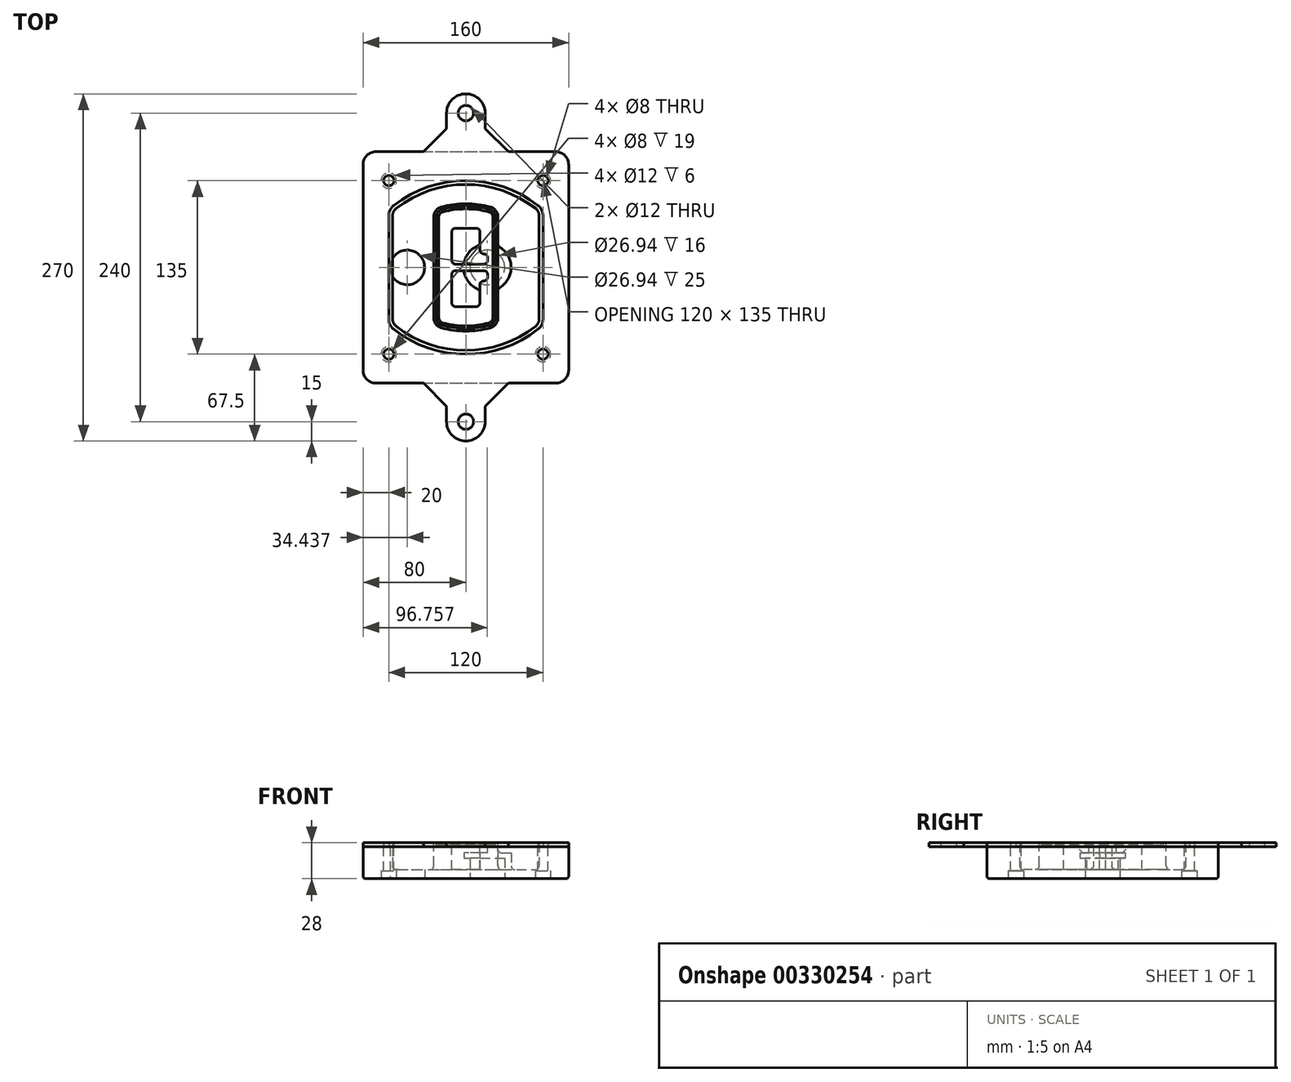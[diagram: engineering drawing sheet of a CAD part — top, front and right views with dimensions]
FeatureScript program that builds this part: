
annotation { "Feature Type Name" : "Feature", "Feature Type Description" : "" }
export const myFeature = defineFeature(function(context is Context, id is Id, definition is map)
    precondition{}
    {
        {
            var Q0;
            Q0=qCreatedBy(makeId("Top.planeOp"),FACE);
            var sketch = newSketch(context, id + "F0", { "sketchPlane" : qUnion([Q0])});
            skPoint(sketch, "E0.rect.middle", {"position": v(0, 0) * mm});
            skLineSegment(sketch, "E1.bottom", {"start": v(-70, -90) * mm, "end": v(70, -90) * mm});
            skLineSegment(sketch, "E1.top", {"start": v(-70, 90) * mm, "end": v(70, 90) * mm});
            skLineSegment(sketch, "E1.left", {"start": v(-80, -80) * mm, "end": v(-80, 80) * mm});
            skLineSegment(sketch, "E1.right", {"start": v(80, -80) * mm, "end": v(80, 80) * mm});
            skLineSegment(sketch, "E2", {"start": v(-80, 90) * mm, "end": v(80, -90) * mm, "construction": true});
            skLineSegment(sketch, "E3", {"start": v(80, 90) * mm, "end": v(-80, -90) * mm, "construction": true});
            skCircle(sketch, "E4", {"center": v(-60, 67.5) * mm, "radius": 4 * mm});
            skCircle(sketch, "E5", {"center": v(60, 67.5) * mm, "radius": 4 * mm});
            skCircle(sketch, "E6", {"center": v(60, -67.5) * mm, "radius": 4 * mm});
            skCircle(sketch, "E7", {"center": v(-60, -67.5) * mm, "radius": 4 * mm});
            skLineSegment(sketch, "E8", {"start": v(-60, 67.5) * mm, "end": v(60, 67.5) * mm, "construction": true});
            skLineSegment(sketch, "E9", {"start": v(60, 67.5) * mm, "end": v(60, -67.5) * mm, "construction": true});
            skLineSegment(sketch, "E10", {"start": v(60, -67.5) * mm, "end": v(-60, -67.5) * mm, "construction": true});
            skLineSegment(sketch, "E11", {"start": v(-60, -67.5) * mm, "end": v(-60, 67.5) * mm, "construction": true});
            skLineSegment(sketch, "E12", {"start": v(-60, 40.3) * mm, "end": v(-60, -40.3) * mm});
            skLineSegment(sketch, "E13", {"start": v(60, 40.3) * mm, "end": v(60, -40.3) * mm});
            skArc(sketch, "E14", {"start": v(56.15, 48.18) * mm, "mid": v(0, 67.5) * mm, "end": v(-56.15, 48.18) * mm});
            skArc(sketch, "E15", {"start": v(-56.15, -48.18) * mm, "mid": v(0, -67.5) * mm, "end": v(56.15, -48.18) * mm});
            skLineSegment(sketch, "E16", {"start": v(-60, 0) * mm, "end": v(60, 0) * mm, "construction": true});
            skPoint(sketch, "E17.visualSharp", {"position": v(-60, -45) * mm});
            skArc(sketch, "E17.filletArc", {"start": v(-60, -40.3) * mm, "mid": v(-58.99, -44.68) * mm, "end": v(-56.15, -48.18) * mm});
            skPoint(sketch, "E18.visualSharp", {"position": v(-60, 45) * mm});
            skArc(sketch, "E18.filletArc", {"start": v(-56.15, 48.18) * mm, "mid": v(-58.99, 44.68) * mm, "end": v(-60, 40.3) * mm});
            skPoint(sketch, "E19.visualSharp", {"position": v(60, 45) * mm});
            skArc(sketch, "E19.filletArc", {"start": v(60, 40.3) * mm, "mid": v(58.99, 44.68) * mm, "end": v(56.15, 48.18) * mm});
            skPoint(sketch, "E20.visualSharp", {"position": v(60, -45) * mm});
            skArc(sketch, "E20.filletArc", {"start": v(56.15, -48.18) * mm, "mid": v(58.99, -44.68) * mm, "end": v(60, -40.3) * mm});
            skPoint(sketch, "E21.visualSharp", {"position": v(-80, 90) * mm});
            skArc(sketch, "E21.filletArc", {"start": v(-70, 90) * mm, "mid": v(-77.07, 87.07) * mm, "end": v(-80, 80) * mm});
            skPoint(sketch, "E22.visualSharp", {"position": v(80, 90) * mm});
            skArc(sketch, "E22.filletArc", {"start": v(80, 80) * mm, "mid": v(77.07, 87.07) * mm, "end": v(70, 90) * mm});
            skPoint(sketch, "E23.visualSharp", {"position": v(80, -90) * mm});
            skArc(sketch, "E23.filletArc", {"start": v(70, -90) * mm, "mid": v(77.07, -87.07) * mm, "end": v(80, -80) * mm});
            skPoint(sketch, "E24.visualSharp", {"position": v(-80, -90) * mm});
            skArc(sketch, "E24.filletArc", {"start": v(-80, -80) * mm, "mid": v(-77.07, -87.07) * mm, "end": v(-70, -90) * mm});
            skArc(sketch, "E25.0", {"start": v(57, 40.3) * mm, "mid": v(56.3, 43.36) * mm, "end": v(54.3, 45.81) * mm});
            skLineSegment(sketch, "E25.1", {"start": v(57, 40.3) * mm, "end": v(57, -40.3) * mm});
            skArc(sketch, "E25.2", {"start": v(54.3, -45.81) * mm, "mid": v(56.3, -43.36) * mm, "end": v(57, -40.3) * mm});
            skArc(sketch, "E25.3", {"start": v(-54.3, -45.81) * mm, "mid": v(0, -64.5) * mm, "end": v(54.3, -45.81) * mm});
            skArc(sketch, "E25.4", {"start": v(-57, -40.3) * mm, "mid": v(-56.3, -43.36) * mm, "end": v(-54.3, -45.81) * mm});
            skArc(sketch, "E25.5", {"start": v(54.3, 45.81) * mm, "mid": v(0, 64.5) * mm, "end": v(-54.3, 45.81) * mm});
            skLineSegment(sketch, "E25.6", {"start": v(-57, 40.3) * mm, "end": v(-57, -40.3) * mm});
            skArc(sketch, "E25.7", {"start": v(-54.3, 45.81) * mm, "mid": v(-56.3, 43.36) * mm, "end": v(-57, 40.3) * mm});
            skArc(sketch, "E26.0", {"start": v(-58.62, 51.33) * mm, "mid": v(-62.58, 46.43) * mm, "end": v(-64, 40.3) * mm});
            skArc(sketch, "E26.1", {"start": v(58.62, 51.33) * mm, "mid": v(0, 71.5) * mm, "end": v(-58.62, 51.33) * mm});
            skArc(sketch, "E26.2", {"start": v(64, 40.3) * mm, "mid": v(62.58, 46.43) * mm, "end": v(58.62, 51.33) * mm});
            skLineSegment(sketch, "E26.3", {"start": v(64, 40.3) * mm, "end": v(64, -40.3) * mm});
            skArc(sketch, "E26.4", {"start": v(58.62, -51.33) * mm, "mid": v(62.58, -46.43) * mm, "end": v(64, -40.3) * mm});
            skLineSegment(sketch, "E26.5", {"start": v(-64, 40.3) * mm, "end": v(-64, -40.3) * mm});
            skArc(sketch, "E26.6", {"start": v(-58.62, -51.33) * mm, "mid": v(0, -71.5) * mm, "end": v(58.62, -51.33) * mm});
            skArc(sketch, "E26.7", {"start": v(-64, -40.3) * mm, "mid": v(-62.58, -46.43) * mm, "end": v(-58.62, -51.33) * mm});
            skSolve(sketch);
        }
        {
            var Q0;
            Q0=makeQuery(id+"F0.imprint","IMPRINT",FACE,{"disambiguationData":[TD([[makeQuery(id+"F0.imprint","IMPRINT",EDGE,{"derivedFrom":sQuery(id+"F0.wireOp",EDGE,"E1.bottom")}),1.0]])]});
            var Q1;
            Q1=makeQuery(id+"F0.imprint","IMPRINT",FACE,{"disambiguationData":[TD([[makeQuery(id+"F0.imprint","IMPRINT",EDGE,{"derivedFrom":sQuery(id+"F0.wireOp",EDGE,"E12")}),1.0]])]});
            var Q2;
            Q2=makeQuery(id+"F0.imprint","IMPRINT",FACE,{"disambiguationData":[TD([[makeQuery(id+"F0.imprint","IMPRINT",EDGE,{"derivedFrom":sQuery(id+"F0.wireOp",EDGE,"E25.0")}),1.0]])]});
            var Q3;
            Q3=makeQuery(id+"F0.imprint","IMPRINT",FACE,{"disambiguationData":[TD([[makeQuery(id+"F0.imprint","IMPRINT",EDGE,{"derivedFrom":sQuery(id+"F0.wireOp",EDGE,"E12")}),-1.0]])]});
            extrude(context, id + "F1", {"entities" : qUnion([Q0, Q1, Q2, Q3]), "oppositeDirection" : true, "depth" : 25 * mm});
        }
        {
            var Q0;
            Q0=makeQuery(id+"F0.imprint","IMPRINT",FACE,{"disambiguationData":[TD([[makeQuery(id+"F0.imprint","IMPRINT",EDGE,{"derivedFrom":sQuery(id+"F0.wireOp",EDGE,"E12")}),1.0]])]});
            extrude(context, id + "F2", {"entities" : qUnion([Q0]), "operationType" : NewBodyOperationType.ADD, "depth" : 3 * mm});
        }
        {
            var Q0;
            Q0=makeQuery(id+"F0.imprint","IMPRINT",FACE,{"disambiguationData":[TD([[makeQuery(id+"F0.imprint","IMPRINT",EDGE,{"derivedFrom":sQuery(id+"F0.wireOp",EDGE,"E25.0")}),1.0]])]});
            extrude(context, id + "F3", {"entities" : qUnion([Q0]), "operationType" : NewBodyOperationType.REMOVE, "oppositeDirection" : true, "depth" : 18 * mm});
        }
        {
            var Q0;
            Q0=makeQuery(id+"F2.opExtrude","CAP_FACE",FACE,{"disambiguationData":[OSD([sQuery(id+"F0.wireOp",EDGE,"E12"),sQuery(id+"F0.wireOp",EDGE,"E13"),sQuery(id+"F0.wireOp",EDGE,"E14"),sQuery(id+"F0.wireOp",EDGE,"E15"),sQuery(id+"F0.wireOp",EDGE,"E17.filletArc"),sQuery(id+"F0.wireOp",EDGE,"E18.filletArc"),sQuery(id+"F0.wireOp",EDGE,"E19.filletArc"),sQuery(id+"F0.wireOp",EDGE,"E20.filletArc"),sQuery(id+"F0.wireOp",EDGE,"E25.0"),sQuery(id+"F0.wireOp",EDGE,"E25.1"),sQuery(id+"F0.wireOp",EDGE,"E25.2"),sQuery(id+"F0.wireOp",EDGE,"E25.3"),sQuery(id+"F0.wireOp",EDGE,"E25.4"),sQuery(id+"F0.wireOp",EDGE,"E25.5"),sQuery(id+"F0.wireOp",EDGE,"E25.6"),sQuery(id+"F0.wireOp",EDGE,"E25.7")])],"isStart":false});
            var sketch = newSketch(context, id + "F4", { "sketchPlane" : qUnion([Q0])});
            skArc(sketch, "E27.0", {"start": v(-19.08, -46.97) * mm, "mid": v(0, -49.5) * mm, "end": v(19.08, -46.97) * mm});
            skArc(sketch, "E28.0", {"start": v(19.08, 46.97) * mm, "mid": v(0, 49.5) * mm, "end": v(-19.08, 46.97) * mm});
            skLineSegment(sketch, "E29", {"start": v(-25, 39.25) * mm, "end": v(-25, -39.25) * mm});
            skLineSegment(sketch, "E30", {"start": v(25, 39.25) * mm, "end": v(25, -39.25) * mm});
            skLineSegment(sketch, "E31", {"start": v(-25, 45.1) * mm, "end": v(25, 45.1) * mm, "construction": true});
            skLineSegment(sketch, "E32", {"start": v(-25, -45.1) * mm, "end": v(25, -45.1) * mm, "construction": true});
            skPoint(sketch, "E33.visualSharp", {"position": v(-25, 45.1) * mm});
            skArc(sketch, "E33.filletArc", {"start": v(-19.08, 46.97) * mm, "mid": v(-23.35, 44.11) * mm, "end": v(-25, 39.25) * mm});
            skPoint(sketch, "E34.visualSharp", {"position": v(25, 45.1) * mm});
            skArc(sketch, "E34.filletArc", {"start": v(25, 39.25) * mm, "mid": v(23.35, 44.11) * mm, "end": v(19.08, 46.97) * mm});
            skPoint(sketch, "E35.visualSharp", {"position": v(25, -45.1) * mm});
            skArc(sketch, "E35.filletArc", {"start": v(19.08, -46.97) * mm, "mid": v(23.35, -44.11) * mm, "end": v(25, -39.25) * mm});
            skPoint(sketch, "E36.visualSharp", {"position": v(-25, -45.1) * mm});
            skArc(sketch, "E36.filletArc", {"start": v(-25, -39.25) * mm, "mid": v(-23.35, -44.11) * mm, "end": v(-19.08, -46.97) * mm});
            skArc(sketch, "E37.0", {"start": v(54.3, 45.81) * mm, "mid": v(0, 64.5) * mm, "end": v(-54.3, 45.81) * mm});
            skArc(sketch, "E37.1", {"start": v(-54.3, 45.81) * mm, "mid": v(-56.3, 43.36) * mm, "end": v(-57, 40.3) * mm});
            skLineSegment(sketch, "E37.2", {"start": v(-57, 40.3) * mm, "end": v(-57, -40.3) * mm});
            skArc(sketch, "E37.3", {"start": v(-57, -40.3) * mm, "mid": v(-56.3, -43.36) * mm, "end": v(-54.3, -45.81) * mm});
            skArc(sketch, "E37.4", {"start": v(-54.3, -45.81) * mm, "mid": v(0, -64.5) * mm, "end": v(54.3, -45.81) * mm});
            skArc(sketch, "E37.5", {"start": v(54.3, -45.81) * mm, "mid": v(56.3, -43.36) * mm, "end": v(57, -40.3) * mm});
            skLineSegment(sketch, "E37.6", {"start": v(57, 40.3) * mm, "end": v(57, -40.3) * mm});
            skArc(sketch, "E37.7", {"start": v(57, 40.3) * mm, "mid": v(56.3, 43.36) * mm, "end": v(54.3, 45.81) * mm});
            skLineSegment(sketch, "E38.0", {"start": v(23, 39.25) * mm, "end": v(23, -39.25) * mm});
            skArc(sketch, "E38.1", {"start": v(18.56, -45.04) * mm, "mid": v(21.76, -42.9) * mm, "end": v(23, -39.25) * mm});
            skArc(sketch, "E38.2", {"start": v(-18.56, -45.04) * mm, "mid": v(0, -47.5) * mm, "end": v(18.56, -45.04) * mm});
            skArc(sketch, "E38.3", {"start": v(-23, -39.25) * mm, "mid": v(-21.76, -42.9) * mm, "end": v(-18.56, -45.04) * mm});
            skLineSegment(sketch, "E38.4", {"start": v(-23, 39.25) * mm, "end": v(-23, -39.25) * mm});
            skArc(sketch, "E38.5", {"start": v(23, 39.25) * mm, "mid": v(21.76, 42.9) * mm, "end": v(18.56, 45.04) * mm});
            skArc(sketch, "E38.6", {"start": v(-18.56, 45.04) * mm, "mid": v(-21.76, 42.9) * mm, "end": v(-23, 39.25) * mm});
            skArc(sketch, "E38.7", {"start": v(18.56, 45.04) * mm, "mid": v(0, 47.5) * mm, "end": v(-18.56, 45.04) * mm});
            skArc(sketch, "E39.0", {"start": v(21, 39.25) * mm, "mid": v(20.18, 41.68) * mm, "end": v(18.04, 43.1) * mm});
            skLineSegment(sketch, "E39.1", {"start": v(21, 39.25) * mm, "end": v(21, -39.25) * mm});
            skArc(sketch, "E39.2", {"start": v(18.04, -43.1) * mm, "mid": v(20.18, -41.68) * mm, "end": v(21, -39.25) * mm});
            skArc(sketch, "E39.3", {"start": v(-18.04, -43.1) * mm, "mid": v(0, -45.5) * mm, "end": v(18.04, -43.1) * mm});
            skArc(sketch, "E39.4", {"start": v(-21, -39.25) * mm, "mid": v(-20.18, -41.68) * mm, "end": v(-18.04, -43.1) * mm});
            skArc(sketch, "E39.5", {"start": v(18.04, 43.1) * mm, "mid": v(0, 45.5) * mm, "end": v(-18.04, 43.1) * mm});
            skLineSegment(sketch, "E39.6", {"start": v(-21, 39.25) * mm, "end": v(-21, -39.25) * mm});
            skArc(sketch, "E39.7", {"start": v(-18.04, 43.1) * mm, "mid": v(-20.18, 41.68) * mm, "end": v(-21, 39.25) * mm});
            skLineSegment(sketch, "E40", {"start": v(-25, 0) * mm, "end": v(25, 0) * mm, "construction": true});
            skLineSegment(sketch, "E41", {"start": v(-11, 5.5) * mm, "end": v(-11, 27.5) * mm});
            skLineSegment(sketch, "E42", {"start": v(-8, 30.5) * mm, "end": v(8, 30.5) * mm});
            skLineSegment(sketch, "E43", {"start": v(11, 27.5) * mm, "end": v(11, 13.5) * mm});
            skLineSegment(sketch, "E44", {"start": v(14, 10.5) * mm, "end": v(14, 10.5) * mm});
            skLineSegment(sketch, "E45", {"start": v(17, 7.5) * mm, "end": v(17, 5.5) * mm});
            skLineSegment(sketch, "E46", {"start": v(14, 2.5) * mm, "end": v(-8, 2.5) * mm});
            skPoint(sketch, "E47.visualSharp", {"position": v(-11, 30.5) * mm});
            skArc(sketch, "E47.filletArc", {"start": v(-8, 30.5) * mm, "mid": v(-10.12, 29.62) * mm, "end": v(-11, 27.5) * mm});
            skPoint(sketch, "E48.visualSharp", {"position": v(11, 30.5) * mm});
            skArc(sketch, "E48.filletArc", {"start": v(11, 27.5) * mm, "mid": v(10.12, 29.62) * mm, "end": v(8, 30.5) * mm});
            skPoint(sketch, "E49.visualSharp", {"position": v(11, 10.5) * mm});
            skArc(sketch, "E49.filletArc", {"start": v(11, 13.5) * mm, "mid": v(11.88, 11.38) * mm, "end": v(14, 10.5) * mm});
            skPoint(sketch, "E50.visualSharp", {"position": v(17, 10.5) * mm});
            skArc(sketch, "E50.filletArc", {"start": v(17, 7.5) * mm, "mid": v(16.12, 9.62) * mm, "end": v(14, 10.5) * mm});
            skPoint(sketch, "E51.visualSharp", {"position": v(17, 2.5) * mm});
            skArc(sketch, "E51.filletArc", {"start": v(14, 2.5) * mm, "mid": v(16.12, 3.38) * mm, "end": v(17, 5.5) * mm});
            skPoint(sketch, "E52.visualSharp", {"position": v(-11, 2.5) * mm});
            skArc(sketch, "E52.filletArc", {"start": v(-11, 5.5) * mm, "mid": v(-10.12, 3.38) * mm, "end": v(-8, 2.5) * mm});
            skLineSegment(sketch, "E53.0.MirrorCS", {"start": v(14, -2.5) * mm, "end": v(-8, -2.5) * mm});
            skArc(sketch, "E54.0.MirrorCS", {"start": v(-11, -5.5) * mm, "mid": v(-10.12, -3.38) * mm, "end": v(-8, -2.5) * mm});
            skLineSegment(sketch, "E55.0.MirrorCS", {"start": v(-11, -5.5) * mm, "end": v(-11, -27.5) * mm});
            skArc(sketch, "E56.0.MirrorCS", {"start": v(-8, -30.5) * mm, "mid": v(-10.12, -29.62) * mm, "end": v(-11, -27.5) * mm});
            skLineSegment(sketch, "E57.0.MirrorCS", {"start": v(-8, -30.5) * mm, "end": v(8, -30.5) * mm});
            skArc(sketch, "E58.0.MirrorCS", {"start": v(11, -27.5) * mm, "mid": v(10.12, -29.62) * mm, "end": v(8, -30.5) * mm});
            skLineSegment(sketch, "E59.0.MirrorCS", {"start": v(11, -27.5) * mm, "end": v(11, -13.5) * mm});
            skArc(sketch, "E60.0.MirrorCS", {"start": v(11, -13.5) * mm, "mid": v(11.88, -11.38) * mm, "end": v(14, -10.5) * mm});
            skArc(sketch, "E61.0.MirrorCS", {"start": v(17, -7.5) * mm, "mid": v(16.12, -9.62) * mm, "end": v(14, -10.5) * mm});
            skLineSegment(sketch, "E62.0.MirrorCS", {"start": v(17, -7.5) * mm, "end": v(17, -5.5) * mm});
            skArc(sketch, "E63.0.MirrorCS", {"start": v(14, -2.5) * mm, "mid": v(16.12, -3.38) * mm, "end": v(17, -5.5) * mm});
            skSolve(sketch);
        }
        {
            var Q0;
            Q0=makeQuery(id+"F4.imprint","IMPRINT",FACE,{"disambiguationData":[TD([[makeQuery(id+"F4.imprint","IMPRINT",EDGE,{"derivedFrom":sQuery(id+"F4.wireOp",EDGE,"E27.0")}),1.0]])]});
            var Q1;
            Q1=makeQuery(id+"F4.imprint","IMPRINT",FACE,{"disambiguationData":[TD([[makeQuery(id+"F4.imprint","IMPRINT",EDGE,{"derivedFrom":sQuery(id+"F4.wireOp",EDGE,"E38.0")}),-1.0]])]});
            var Q2;
            Q2=makeQuery(id+"F4.imprint","IMPRINT",FACE,{"disambiguationData":[TD([[makeQuery(id+"F4.imprint","IMPRINT",EDGE,{"derivedFrom":sQuery(id+"F4.wireOp",EDGE,"E39.0")}),1.0]])]});
            extrude(context, id + "F5", {"entities" : qUnion([Q0, Q1, Q2]), "operationType" : NewBodyOperationType.ADD, "endBound" : BoundingType.UP_TO_NEXT, "oppositeDirection" : true, "depth" : 25 * mm});
        }
        {
            var Q0;
            Q0=makeQuery(id+"F4.imprint","IMPRINT",FACE,{"disambiguationData":[TD([[makeQuery(id+"F4.imprint","IMPRINT",EDGE,{"derivedFrom":sQuery(id+"F4.wireOp",EDGE,"E38.0")}),-1.0]])]});
            extrude(context, id + "F6", {"entities" : qUnion([Q0]), "operationType" : NewBodyOperationType.REMOVE, "oppositeDirection" : true, "depth" : 2 * mm});
        }
        {
            var Q0;
            Q0=makeQuery(id+"F1.opExtrude","CAP_FACE",FACE,{"disambiguationData":[OSD([sQuery(id+"F0.wireOp",EDGE,"E1.bottom"),sQuery(id+"F0.wireOp",EDGE,"E1.top"),sQuery(id+"F0.wireOp",EDGE,"E1.left"),sQuery(id+"F0.wireOp",EDGE,"E1.right"),sQuery(id+"F0.wireOp",EDGE,"E4"),sQuery(id+"F0.wireOp",EDGE,"E5"),sQuery(id+"F0.wireOp",EDGE,"E6"),sQuery(id+"F0.wireOp",EDGE,"E7"),sQuery(id+"F0.wireOp",EDGE,"E21.filletArc"),sQuery(id+"F0.wireOp",EDGE,"E22.filletArc"),sQuery(id+"F0.wireOp",EDGE,"E23.filletArc"),sQuery(id+"F0.wireOp",EDGE,"E24.filletArc")])],"isStart":false});
            var sketch = newSketch(context, id + "F7", { "sketchPlane" : qUnion([Q0])});
            skCircle(sketch, "E64", {"center": v(16.76, 0) * mm, "radius": 13.47 * mm});
            skCircle(sketch, "E65", {"center": v(-45.56, 0) * mm, "radius": 13.47 * mm});
            skLineSegment(sketch, "E66", {"start": v(80, 0) * mm, "end": v(-80, 0) * mm});
            skCircle(sketch, "E67", {"center": v(16.76, 0) * mm, "radius": 18.47 * mm});
            skCircle(sketch, "E68", {"center": v(60, -67.5) * mm, "radius": 6 * mm});
            skCircle(sketch, "E69", {"center": v(-60, -67.5) * mm, "radius": 6 * mm});
            skCircle(sketch, "E70", {"center": v(-60, 67.5) * mm, "radius": 6 * mm});
            skCircle(sketch, "E71", {"center": v(60, 67.5) * mm, "radius": 6 * mm});
            skSolve(sketch);
        }
        {
            var Q0;
            {var subQ1=sQuery(id+"F7.wireOp",EDGE,"E66");var subQ4=sQuery(id+"F7.wireOp",EDGE,"E64");var subQ6=makeQuery(id+"F7.imprint","INTERSECT",VERTEX,{"disambiguationData":[OD(0.0)],"derivedFrom":[subQ4,subQ1]});Q0=makeQuery(id+"F7.imprint","IMPRINT",FACE,{"disambiguationData":[TD([[makeQuery(id+"F7.imprint","IMPRINT",EDGE,{"disambiguationData":[TD([[subQ6,-1.0]])],"derivedFrom":subQ4}),-1.0]])]});}
            var Q1;
            {var subQ0=sQuery(id+"F7.wireOp",EDGE,"E66");var subQ1=sQuery(id+"F7.wireOp",EDGE,"E64");var subQ3=makeQuery(id+"F7.imprint","INTERSECT",VERTEX,{"disambiguationData":[OD(0.0)],"derivedFrom":[subQ1,subQ0]});Q1=makeQuery(id+"F7.imprint","IMPRINT",FACE,{"disambiguationData":[TD([[makeQuery(id+"F7.imprint","IMPRINT",EDGE,{"disambiguationData":[TD([[subQ3,-1.0]])],"derivedFrom":subQ1}),1.0]])]});}
            var Q2;
            {var subQ0=sQuery(id+"F7.wireOp",EDGE,"E66");var subQ1=sQuery(id+"F7.wireOp",EDGE,"E64");var subQ3=makeQuery(id+"F7.imprint","INTERSECT",VERTEX,{"disambiguationData":[OD(0.0)],"derivedFrom":[subQ1,subQ0]});Q2=makeQuery(id+"F7.imprint","IMPRINT",FACE,{"disambiguationData":[TD([[makeQuery(id+"F7.imprint","IMPRINT",EDGE,{"disambiguationData":[TD([[subQ3,1.0]])],"derivedFrom":subQ1}),1.0]])]});}
            var Q3;
            {var subQ1=sQuery(id+"F7.wireOp",EDGE,"E66");var subQ4=sQuery(id+"F7.wireOp",EDGE,"E64");var subQ6=makeQuery(id+"F7.imprint","INTERSECT",VERTEX,{"disambiguationData":[OD(0.0)],"derivedFrom":[subQ4,subQ1]});Q3=makeQuery(id+"F7.imprint","IMPRINT",FACE,{"disambiguationData":[TD([[makeQuery(id+"F7.imprint","IMPRINT",EDGE,{"disambiguationData":[TD([[subQ6,1.0]])],"derivedFrom":subQ4}),-1.0]])]});}
            extrude(context, id + "F8", {"entities" : qUnion([Q0, Q1, Q2, Q3]), "operationType" : NewBodyOperationType.ADD, "oppositeDirection" : true, "depth" : 20 * mm});
        }
        {
            var Q0;
            {var subQ0=sQuery(id+"F7.wireOp",EDGE,"E66");var subQ1=sQuery(id+"F7.wireOp",EDGE,"E64");var subQ3=makeQuery(id+"F7.imprint","INTERSECT",VERTEX,{"disambiguationData":[OD(0.0)],"derivedFrom":[subQ1,subQ0]});Q0=makeQuery(id+"F7.imprint","IMPRINT",FACE,{"disambiguationData":[TD([[makeQuery(id+"F7.imprint","IMPRINT",EDGE,{"disambiguationData":[TD([[subQ3,-1.0]])],"derivedFrom":subQ1}),1.0]])]});}
            var Q1;
            {var subQ0=sQuery(id+"F7.wireOp",EDGE,"E66");var subQ1=sQuery(id+"F7.wireOp",EDGE,"E64");var subQ3=makeQuery(id+"F7.imprint","INTERSECT",VERTEX,{"disambiguationData":[OD(0.0)],"derivedFrom":[subQ1,subQ0]});Q1=makeQuery(id+"F7.imprint","IMPRINT",FACE,{"disambiguationData":[TD([[makeQuery(id+"F7.imprint","IMPRINT",EDGE,{"disambiguationData":[TD([[subQ3,1.0]])],"derivedFrom":subQ1}),1.0]])]});}
            extrude(context, id + "F9", {"entities" : qUnion([Q0, Q1]), "operationType" : NewBodyOperationType.REMOVE, "oppositeDirection" : true, "depth" : 16 * mm});
        }
        {
            var Q0;
            {var subQ0=sQuery(id+"F7.wireOp",EDGE,"E66");var subQ1=sQuery(id+"F7.wireOp",EDGE,"E65");var subQ3=makeQuery(id+"F7.imprint","INTERSECT",VERTEX,{"disambiguationData":[OD(0.0)],"derivedFrom":[subQ1,subQ0]});Q0=makeQuery(id+"F7.imprint","IMPRINT",FACE,{"disambiguationData":[TD([[makeQuery(id+"F7.imprint","IMPRINT",EDGE,{"disambiguationData":[TD([[subQ3,-1.0]])],"derivedFrom":subQ1}),1.0]])]});}
            var Q1;
            {var subQ0=sQuery(id+"F7.wireOp",EDGE,"E66");var subQ1=sQuery(id+"F7.wireOp",EDGE,"E65");var subQ3=makeQuery(id+"F7.imprint","INTERSECT",VERTEX,{"disambiguationData":[OD(0.0)],"derivedFrom":[subQ1,subQ0]});Q1=makeQuery(id+"F7.imprint","IMPRINT",FACE,{"disambiguationData":[TD([[makeQuery(id+"F7.imprint","IMPRINT",EDGE,{"disambiguationData":[TD([[subQ3,1.0]])],"derivedFrom":subQ1}),1.0]])]});}
            extrude(context, id + "F10", {"entities" : qUnion([Q0, Q1]), "operationType" : NewBodyOperationType.REMOVE, "oppositeDirection" : true, "depth" : 25 * mm});
        }
        {
            var Q0;
            Q0=makeQuery(id+"F7.imprint","IMPRINT",FACE,{"disambiguationData":[TD([[makeQuery(id+"F7.imprint","IMPRINT",EDGE,{"derivedFrom":sQuery(id+"F7.wireOp",EDGE,"E68")}),1.0]])]});
            var Q1;
            Q1=makeQuery(id+"F7.imprint","IMPRINT",FACE,{"disambiguationData":[TD([[makeQuery(id+"F7.imprint","IMPRINT",EDGE,{"derivedFrom":makeQuery(id+"F1.opExtrude","CAP_EDGE",EDGE,{"disambiguationData":[OSD([sQuery(id+"F0.wireOp",EDGE,"E5")])],"isStart":false})}),-1.0]])]});
            var Q2;
            Q2=makeQuery(id+"F7.imprint","IMPRINT",FACE,{"disambiguationData":[TD([[makeQuery(id+"F7.imprint","IMPRINT",EDGE,{"derivedFrom":sQuery(id+"F7.wireOp",EDGE,"E69")}),1.0]])]});
            var Q3;
            Q3=makeQuery(id+"F7.imprint","IMPRINT",FACE,{"disambiguationData":[TD([[makeQuery(id+"F7.imprint","IMPRINT",EDGE,{"derivedFrom":makeQuery(id+"F1.opExtrude","CAP_EDGE",EDGE,{"disambiguationData":[OSD([sQuery(id+"F0.wireOp",EDGE,"E4")])],"isStart":false})}),-1.0]])]});
            var Q4;
            Q4=makeQuery(id+"F7.imprint","IMPRINT",FACE,{"disambiguationData":[TD([[makeQuery(id+"F7.imprint","IMPRINT",EDGE,{"derivedFrom":sQuery(id+"F7.wireOp",EDGE,"E70")}),1.0]])]});
            var Q5;
            Q5=makeQuery(id+"F7.imprint","IMPRINT",FACE,{"disambiguationData":[TD([[makeQuery(id+"F7.imprint","IMPRINT",EDGE,{"derivedFrom":makeQuery(id+"F1.opExtrude","CAP_EDGE",EDGE,{"disambiguationData":[OSD([sQuery(id+"F0.wireOp",EDGE,"E7")])],"isStart":false})}),-1.0]])]});
            var Q6;
            Q6=makeQuery(id+"F7.imprint","IMPRINT",FACE,{"disambiguationData":[TD([[makeQuery(id+"F7.imprint","IMPRINT",EDGE,{"derivedFrom":sQuery(id+"F7.wireOp",EDGE,"E71")}),1.0]])]});
            var Q7;
            Q7=makeQuery(id+"F7.imprint","IMPRINT",FACE,{"disambiguationData":[TD([[makeQuery(id+"F7.imprint","IMPRINT",EDGE,{"derivedFrom":makeQuery(id+"F1.opExtrude","CAP_EDGE",EDGE,{"disambiguationData":[OSD([sQuery(id+"F0.wireOp",EDGE,"E6")])],"isStart":false})}),-1.0]])]});
            extrude(context, id + "F11", {"entities" : qUnion([Q0, Q1, Q2, Q3, Q4, Q5, Q6, Q7]), "operationType" : NewBodyOperationType.REMOVE, "oppositeDirection" : true, "depth" : 6 * mm});
        }
        {
            var Q0;
            Q0=makeQuery(id+"F9.boolean.opBoolean","COPY",FACE,{"derivedFrom":makeQuery(id+"F9.opExtrude","CAP_FACE",FACE,{"disambiguationData":[OSD([sQuery(id+"F7.wireOp",EDGE,"E64")])],"isStart":false})});
            var sketch = newSketch(context, id + "F12", { "sketchPlane" : qUnion([Q0])});
            skArc(sketch, "E72.0", {"start": v(11, 17.55) * mm, "mid": v(2.57, 11.82) * mm, "end": v(-1.54, 2.5) * mm});
            skArc(sketch, "E72.1", {"start": v(-1.54, -2.5) * mm, "mid": v(2.57, -11.82) * mm, "end": v(11, -17.55) * mm});
            skLineSegment(sketch, "E73", {"start": v(-1.54, -2.5) * mm, "end": v(14, -2.5) * mm});
            skLineSegment(sketch, "E74.0", {"start": v(14, 2.5) * mm, "end": v(-1.54, 2.5) * mm});
            skArc(sketch, "E74.1", {"start": v(14, 2.5) * mm, "mid": v(16.12, 3.38) * mm, "end": v(17, 5.5) * mm});
            skLineSegment(sketch, "E74.2", {"start": v(17, 7.5) * mm, "end": v(17, 5.5) * mm});
            skArc(sketch, "E74.3", {"start": v(17, 7.5) * mm, "mid": v(16.12, 9.62) * mm, "end": v(14, 10.5) * mm});
            skArc(sketch, "E74.4", {"start": v(11, 13.5) * mm, "mid": v(11.88, 11.38) * mm, "end": v(14, 10.5) * mm});
            skLineSegment(sketch, "E74.5", {"start": v(11, 17.55) * mm, "end": v(11, 13.5) * mm});
            skLineSegment(sketch, "E74.7", {"start": v(14, -2.5) * mm, "end": v(-1.54, -2.5) * mm});
            skArc(sketch, "E74.8", {"start": v(14, -2.5) * mm, "mid": v(16.12, -3.38) * mm, "end": v(17, -5.5) * mm});
            skLineSegment(sketch, "E74.9", {"start": v(17, -7.5) * mm, "end": v(17, -5.5) * mm});
            skArc(sketch, "E74.10", {"start": v(17, -7.5) * mm, "mid": v(16.12, -9.62) * mm, "end": v(14, -10.5) * mm});
            skArc(sketch, "E74.11", {"start": v(11, -13.5) * mm, "mid": v(11.88, -11.38) * mm, "end": v(14, -10.5) * mm});
            skLineSegment(sketch, "E74.12", {"start": v(11, -17.55) * mm, "end": v(11, -13.5) * mm});
            skPoint(sketch, "E75.orphan", {"position": v(11, -27.5) * mm});
            skPoint(sketch, "E76.orphan", {"position": v(-8, -2.5) * mm});
            skPoint(sketch, "E77.orphan", {"position": v(-8, 2.5) * mm});
            skPoint(sketch, "E78.orphan", {"position": v(11, 27.5) * mm});
            skSolve(sketch);
        }
        {
            var Q0;
            {var subQ7=sQuery(id+"F12.wireOp",EDGE,"E72.0");var subQ14=sQuery(id+"F12.wireOp",EDGE,"E72.1");var subQ16=sQuery(id+"F12.wireOp",EDGE,"E74.1");var subQ18=sQuery(id+"F12.wireOp",EDGE,"E74.8");Q0=qUnion([makeQuery(id+"F12.imprint","IMPRINT",FACE,{"disambiguationData":[TD([[makeQuery(id+"F12.imprint","IMPRINT",EDGE,{"derivedFrom":subQ7}),1.0]])]}),makeQuery(id+"F12.imprint","IMPRINT",FACE,{"disambiguationData":[TD([[makeQuery(id+"F12.imprint","IMPRINT",EDGE,{"derivedFrom":subQ14}),1.0]])]}),makeQuery(id+"F12.imprint","IMPRINT",FACE,{"disambiguationData":[TD([[makeQuery(id+"F12.imprint","IMPRINT",EDGE,{"derivedFrom":subQ16}),1.0]])]}),makeQuery(id+"F12.imprint","IMPRINT",FACE,{"disambiguationData":[TD([[makeQuery(id+"F12.imprint","IMPRINT",EDGE,{"derivedFrom":subQ18}),-1.0]])]})]);}
            var Q1;
            Q1=makeQuery(id+"F5.boolean.opBoolean","SPLIT",FACE,{"disambiguationData":[TD([makeQuery(id+"F5.opExtrude","SWEPT_FACE",FACE,{"disambiguationData":[OSD([sQuery(id+"F4.wireOp",EDGE,"E41")])]})])],"derivedFrom":makeQuery(id+"F3.boolean.opBoolean","COPY",FACE,{"derivedFrom":makeQuery(id+"F3.opExtrude","CAP_FACE",FACE,{"disambiguationData":[OSD([sQuery(id+"F0.wireOp",EDGE,"E25.0"),sQuery(id+"F0.wireOp",EDGE,"E25.1"),sQuery(id+"F0.wireOp",EDGE,"E25.2"),sQuery(id+"F0.wireOp",EDGE,"E25.3"),sQuery(id+"F0.wireOp",EDGE,"E25.4"),sQuery(id+"F0.wireOp",EDGE,"E25.5"),sQuery(id+"F0.wireOp",EDGE,"E25.6"),sQuery(id+"F0.wireOp",EDGE,"E25.7")])],"isStart":false})})});
            extrude(context, id + "F13", {"entities" : qUnion([Q0]), "operationType" : NewBodyOperationType.REMOVE, "endBound" : BoundingType.UP_TO_SURFACE, "endBoundEntityFace" : qUnion([Q1]), "depth" : 25 * mm});
        }
        {
            var Q0;
            Q0=makeQuery(id+"F3.boolean.opBoolean","COPY",EDGE,{"derivedFrom":makeQuery(id+"F3.opExtrude","CAP_EDGE",EDGE,{"disambiguationData":[OSD([sQuery(id+"F0.wireOp",EDGE,"E25.6")])],"isStart":false})});
            var Q1;
            Q1=makeQuery(id+"F8.boolean.opBoolean","INTERSECT",EDGE,{"derivedFrom":[makeQuery(id+"F5.opExtrude","SWEPT_FACE",FACE,{"disambiguationData":[OSD([sQuery(id+"F4.wireOp",EDGE,"E30")])]}),makeQuery(id+"F8.opExtrude","CAP_FACE",FACE,{"disambiguationData":[OSD([sQuery(id+"F7.wireOp",EDGE,"E67")])],"isStart":false})]});
            var Q2;
            Q2=makeQuery(id+"F8.boolean.opBoolean","INTERSECT",EDGE,{"disambiguationData":[OD(1.0)],"derivedFrom":[makeQuery(id+"F5.opExtrude","SWEPT_FACE",FACE,{"disambiguationData":[OSD([sQuery(id+"F4.wireOp",EDGE,"E30")])]}),makeQuery(id+"F8.opExtrude","SWEPT_FACE",FACE,{"disambiguationData":[OSD([sQuery(id+"F7.wireOp",EDGE,"E67")])]})]});
            var Q3;
            {var subQ0=sQuery(id+"F4.wireOp",EDGE,"E30");Q3=makeQuery(id+"F8.boolean.opBoolean","SPLIT",EDGE,{"disambiguationData":[TD([makeQuery(id+"F5.opExtrude","SWEPT_FACE",FACE,{"disambiguationData":[OSD([sQuery(id+"F4.wireOp",EDGE,"E35.filletArc")])]})])],"derivedFrom":makeQuery(id+"F5.opExtrude","CAP_EDGE",EDGE,{"disambiguationData":[OSD([subQ0])],"isStart":false})});}
            var Q4;
            {var subQ0=sQuery(id+"F0.wireOp",EDGE,"E25.7");var subQ1=sQuery(id+"F0.wireOp",EDGE,"E25.1");var subQ2=sQuery(id+"F0.wireOp",EDGE,"E25.6");var subQ3=sQuery(id+"F0.wireOp",EDGE,"E25.5");var subQ4=sQuery(id+"F0.wireOp",EDGE,"E25.4");var subQ5=sQuery(id+"F0.wireOp",EDGE,"E25.0");var subQ6=sQuery(id+"F0.wireOp",EDGE,"E25.2");var subQ7=sQuery(id+"F0.wireOp",EDGE,"E25.3");Q4=makeQuery(id+"F8.boolean.opBoolean","INTERSECT",EDGE,{"derivedFrom":[makeQuery(id+"F5.boolean.opBoolean","SPLIT",FACE,{"disambiguationData":[TD([makeQuery(id+"F2.opExtrude","SWEPT_FACE",FACE,{"disambiguationData":[OSD([subQ5])]})])],"derivedFrom":makeQuery(id+"F3.boolean.opBoolean","COPY",FACE,{"derivedFrom":makeQuery(id+"F3.opExtrude","CAP_FACE",FACE,{"disambiguationData":[OSD([subQ5,subQ1,subQ6,subQ7,subQ4,subQ3,subQ2,subQ0])],"isStart":false})})}),makeQuery(id+"F8.opExtrude","SWEPT_FACE",FACE,{"disambiguationData":[OSD([sQuery(id+"F7.wireOp",EDGE,"E67")])]})]});}
            var Q5;
            Q5=makeQuery(id+"F8.boolean.opBoolean","INTERSECT",EDGE,{"disambiguationData":[OD(0.0)],"derivedFrom":[makeQuery(id+"F5.opExtrude","SWEPT_FACE",FACE,{"disambiguationData":[OSD([sQuery(id+"F4.wireOp",EDGE,"E30")])]}),makeQuery(id+"F8.opExtrude","SWEPT_FACE",FACE,{"disambiguationData":[OSD([sQuery(id+"F7.wireOp",EDGE,"E67")])]})]});
            fillet(context, id + "F14", {"entities" : qUnion([Q0, Q1, Q2, Q3, Q4, Q5]), "radius" : 3 * mm, "tangentPropagation" : true, "allowEdgeOverflow" : false});
        }
        {
            var Q0;
            Q0=makeQuery(id+"F1.opExtrude","CAP_EDGE",EDGE,{"disambiguationData":[OSD([sQuery(id+"F0.wireOp",EDGE,"E1.bottom")])],"isStart":false});
            fillet(context, id + "F15", {"entities" : qUnion([Q0]), "radius" : 2 * mm, "tangentPropagation" : true, "allowEdgeOverflow" : false});
        }
        {
            var Q0;
            {var subQ0=sQuery(id+"F0.wireOp",EDGE,"E21.filletArc");var subQ1=sQuery(id+"F0.wireOp",EDGE,"E7");var subQ2=sQuery(id+"F0.wireOp",EDGE,"E6");var subQ3=sQuery(id+"F0.wireOp",EDGE,"E5");var subQ4=sQuery(id+"F0.wireOp",EDGE,"E4");var subQ5=sQuery(id+"F0.wireOp",EDGE,"E22.filletArc");var subQ6=sQuery(id+"F0.wireOp",EDGE,"E1.bottom");var subQ7=sQuery(id+"F0.wireOp",EDGE,"E1.right");var subQ8=sQuery(id+"F0.wireOp",EDGE,"E1.top");var subQ9=sQuery(id+"F0.wireOp",EDGE,"E1.left");var subQ10=sQuery(id+"F0.wireOp",EDGE,"E23.filletArc");var subQ11=sQuery(id+"F0.wireOp",EDGE,"E24.filletArc");Q0=makeQuery(id+"F2.boolean.opBoolean","SPLIT",FACE,{"disambiguationData":[TD([makeQuery(id+"F1.opExtrude","SWEPT_FACE",FACE,{"disambiguationData":[OSD([subQ6])]})])],"derivedFrom":makeQuery(id+"F1.opExtrude","CAP_FACE",FACE,{"disambiguationData":[OSD([subQ6,subQ8,subQ9,subQ7,subQ4,subQ3,subQ2,subQ1,subQ0,subQ5,subQ10,subQ11])],"isStart":true})});}
            var sketch = newSketch(context, id + "F16", { "sketchPlane" : qUnion([Q0])});
            skLineSegment(sketch, "E79.0", {"start": v(-60, 40.3) * mm, "end": v(-60, -40.3) * mm});
            skLineSegment(sketch, "E80.0", {"start": v(-80, -80) * mm, "end": v(-80, 80) * mm});
            skPoint(sketch, "E81.0", {"position": v(60, 0) * mm});
            skLineSegment(sketch, "E82.0", {"start": v(-70, 90) * mm, "end": v(70, 90) * mm});
            skLineSegment(sketch, "E83.0", {"start": v(60, 40.3) * mm, "end": v(60, -40.3) * mm});
            skArc(sketch, "E83.1", {"start": v(60, 40.3) * mm, "mid": v(58.99, 44.68) * mm, "end": v(56.15, 48.18) * mm});
            skArc(sketch, "E83.3", {"start": v(-56.15, 48.18) * mm, "mid": v(-58.99, 44.68) * mm, "end": v(-60, 40.3) * mm});
            skArc(sketch, "E83.4", {"start": v(56.15, 48.18) * mm, "mid": v(0, 67.5) * mm, "end": v(-56.15, 48.18) * mm});
            skArc(sketch, "E83.5", {"start": v(56.15, -48.18) * mm, "mid": v(58.99, -44.68) * mm, "end": v(60, -40.3) * mm});
            skArc(sketch, "E83.6", {"start": v(-56.15, -48.18) * mm, "mid": v(0, -67.5) * mm, "end": v(56.15, -48.18) * mm});
            skArc(sketch, "E83.7", {"start": v(-60, -40.3) * mm, "mid": v(-58.99, -44.68) * mm, "end": v(-56.15, -48.18) * mm});
            skArc(sketch, "E84.0", {"start": v(80, 80) * mm, "mid": v(77.07, 87.07) * mm, "end": v(70, 90) * mm});
            skLineSegment(sketch, "E84.1", {"start": v(80, -80) * mm, "end": v(80, 80) * mm});
            skArc(sketch, "E84.2", {"start": v(70, -90) * mm, "mid": v(77.07, -87.07) * mm, "end": v(80, -80) * mm});
            skArc(sketch, "E84.3", {"start": v(-80, -80) * mm, "mid": v(-77.07, -87.07) * mm, "end": v(-70, -90) * mm});
            skArc(sketch, "E85.0", {"start": v(-70, 90) * mm, "mid": v(-77.07, 87.07) * mm, "end": v(-80, 80) * mm});
            skLineSegment(sketch, "E85.1", {"start": v(-70, -90) * mm, "end": v(70, -90) * mm});
            skCircle(sketch, "E85.2", {"center": v(-60, -67.5) * mm, "radius": 4 * mm});
            skCircle(sketch, "E85.3", {"center": v(-60, 67.5) * mm, "radius": 4 * mm});
            skCircle(sketch, "E85.4", {"center": v(60, 67.5) * mm, "radius": 4 * mm});
            skCircle(sketch, "E85.5", {"center": v(60, -67.5) * mm, "radius": 4 * mm});
            skLineSegment(sketch, "E86", {"start": v(0, 90) * mm, "end": v(0, 120) * mm, "construction": true});
            skPoint(sketch, "E86.endSnap0", {"position": v(0, 90) * mm});
            skArc(sketch, "E87", {"start": v(15, 120) * mm, "mid": v(0, 135) * mm, "end": v(-15, 120) * mm});
            skLineSegment(sketch, "E88", {"start": v(-15, 120) * mm, "end": v(-15, 108) * mm});
            skLineSegment(sketch, "E89", {"start": v(-15, 108) * mm, "end": v(-33, 90) * mm});
            skArc(sketch, "E90.MirrorCS", {"start": v(-15, 120) * mm, "mid": v(0, 135) * mm, "end": v(15, 120) * mm});
            skLineSegment(sketch, "E91.MirrorCS", {"start": v(15, 120) * mm, "end": v(15, 108) * mm});
            skLineSegment(sketch, "E92.MirrorCS", {"start": v(15, 108) * mm, "end": v(33, 90) * mm});
            skCircle(sketch, "E93", {"center": v(0, 120) * mm, "radius": 6 * mm});
            skLineSegment(sketch, "E94", {"start": v(101.99, 0) * mm, "end": v(-89.5, 0) * mm, "construction": true});
            skArc(sketch, "E95.MirrorCS", {"start": v(15, -120) * mm, "mid": v(0, -135) * mm, "end": v(-15, -120) * mm});
            skCircle(sketch, "E96.MirrorC", {"center": v(0, -120) * mm, "radius": 6 * mm});
            skLineSegment(sketch, "E97.MirrorCS", {"start": v(15, -120) * mm, "end": v(15, -108) * mm});
            skLineSegment(sketch, "E98.MirrorCS", {"start": v(-15, -120) * mm, "end": v(-15, -108) * mm});
            skArc(sketch, "E99.MirrorCS", {"start": v(-15, -120) * mm, "mid": v(0, -135) * mm, "end": v(15, -120) * mm});
            skLineSegment(sketch, "E100.MirrorCS", {"start": v(-15, -108) * mm, "end": v(-33, -90) * mm});
            skPoint(sketch, "E101.MirrorP", {"position": v(0, -90) * mm});
            skLineSegment(sketch, "E102.MirrorCS", {"start": v(0, -90) * mm, "end": v(0, -120) * mm, "construction": true});
            skLineSegment(sketch, "E103.MirrorCS", {"start": v(15, -108) * mm, "end": v(33, -90) * mm});
            skSolve(sketch);
        }
        {
            var Q0;
            Q0=makeQuery(id+"F16.imprint","IMPRINT",FACE,{"disambiguationData":[TD([[makeQuery(id+"F16.imprint","IMPRINT",EDGE,{"derivedFrom":sQuery(id+"F16.wireOp",EDGE,"E79.0")}),-1.0]])]});
            var Q1;
            {var subQ1=sQuery(id+"F16.wireOp",EDGE,"E100.MirrorCS");Q1=makeQuery(id+"F16.imprint","IMPRINT",FACE,{"disambiguationData":[TD([[makeQuery(id+"F16.imprint","IMPRINT",EDGE,{"derivedFrom":subQ1}),-1.0]])]});}
            var Q2;
            Q2=makeQuery(id+"F16.imprint","IMPRINT",FACE,{"disambiguationData":[TD([[makeQuery(id+"F16.imprint","IMPRINT",EDGE,{"derivedFrom":sQuery(id+"F16.wireOp",EDGE,"E88")}),1.0]])]});
            var Q3;
            Q3=makeQuery(id+"F2.opExtrude","CAP_FACE",FACE,{"disambiguationData":[OSD([sQuery(id+"F0.wireOp",EDGE,"E12"),sQuery(id+"F0.wireOp",EDGE,"E13"),sQuery(id+"F0.wireOp",EDGE,"E14"),sQuery(id+"F0.wireOp",EDGE,"E15"),sQuery(id+"F0.wireOp",EDGE,"E17.filletArc"),sQuery(id+"F0.wireOp",EDGE,"E18.filletArc"),sQuery(id+"F0.wireOp",EDGE,"E19.filletArc"),sQuery(id+"F0.wireOp",EDGE,"E20.filletArc"),sQuery(id+"F0.wireOp",EDGE,"E25.0"),sQuery(id+"F0.wireOp",EDGE,"E25.1"),sQuery(id+"F0.wireOp",EDGE,"E25.2"),sQuery(id+"F0.wireOp",EDGE,"E25.3"),sQuery(id+"F0.wireOp",EDGE,"E25.4"),sQuery(id+"F0.wireOp",EDGE,"E25.5"),sQuery(id+"F0.wireOp",EDGE,"E25.6"),sQuery(id+"F0.wireOp",EDGE,"E25.7")])],"isStart":false});
            extrude(context, id + "F17", {"entities" : qUnion([Q0, Q1, Q2]), "endBound" : BoundingType.UP_TO_SURFACE, "endBoundEntityFace" : qUnion([Q3]), "depth" : 25 * mm});
        }
    });
